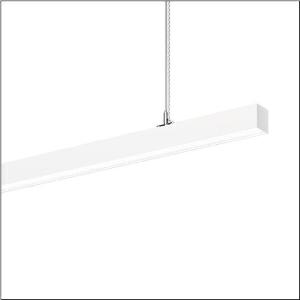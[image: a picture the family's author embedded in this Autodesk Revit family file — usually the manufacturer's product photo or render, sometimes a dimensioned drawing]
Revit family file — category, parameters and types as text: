
# Revit family: silica_r__21_51mx33tat7w_2751
name_source: partatom
category: Lighting Fixtures
units: mm (PartAtom-declared; Revit-internal decimal feet)

## family parameters
Cut with Voids When Loaded = No
Host = Face
Light Source = No
Part Type = Normal
Room Calculation Point = No
Round Connector Dimension = Use Diameter
Shared = No

## types (1)
- --- (1 x LED, 5740 lm, 53.8 W, 6500K)
    Apparent Load = 54 VA
    CIE Flux Codes = 78 96 99 56 100
    Color Rendering = 80
    Color Temperature = 6500K
    Default Elevation = 1800 mm
    Description = Silica® 21, office luminaire, primary optical cover: prismatic diffuser, of PMMA, CAT 2 (L<= 3000cd/m²), light emission: direct/indirect distribution, primary light characteristic: symmetric, installation type: suspended mounting, LED, rated luminous flux: 5.740lm, luminous efficacy: 102lm/W, light colour: 8tw, colour temperature: 2700..6500K, control gear: ECG DALI, with terminal, 3+2-pole, max. 2.5mm², mains connection: 220..240V, AC, 50/60Hz, rated input power: 56.5W, luminaire housing, of aluminium, traffic white (RAL 9016), length: 1.204mm, width: 53mm, height: 53mm, protection rating (complete): IP20, insulation class (complete): insulation class I (protective earthing), certification: CE, permissible operating ambient temperature: 0..+35°C, standard: EN 50419, packaging unit: 1 piece
    Height = 53 mm
    Lamp = 1 x LED
    Lamp Light Flux = 5740 lm
    Lamp Power = 53.8 W
    Lamp count = 1
    Length = 1204 mm
    Luminous efficacy = 107 lm/W
    Manufacturer = Siteco
    ModVariant = No
    Model = 51MX33TAT7W
    Mounting Place = Ceiling
    Mounting Type = Pendant
    Number of Poles = 1
    OnlyDefault = Yes
    Power Factor = 1
    Product Name = Silica® 21
    Product group = office luminaire | ceiling pendant
    ProductGroupID = 902
    Protection Class = Protection class I
    Protection Degree = IP 20
    RLX_Detail_Level = 1
    RLX_Emergency_Light_Flux = 0 lm
    RLX_Emergency_Type = 0
    RLX_Emergency_Type_DB = No
    RlxData = <blob elided: 18185 chars, md5=6d99b95c>
    Socket = socket
    Standby Power = 0 W
    System Light Flux = 5740 lm
    System Power = 54 W
    Type Comments = individual setting
    Type Image = l_1297784.jpg
    URL = http://relux.com
    VarID = @adj_071107
    Voltage = 0 V
    Weight = 0.00 kg
    Width = 53 mm

## geometry (parser evidence)
native form markers: Blend x4, Sweep x13
no freeform markers — native parametric forms only
